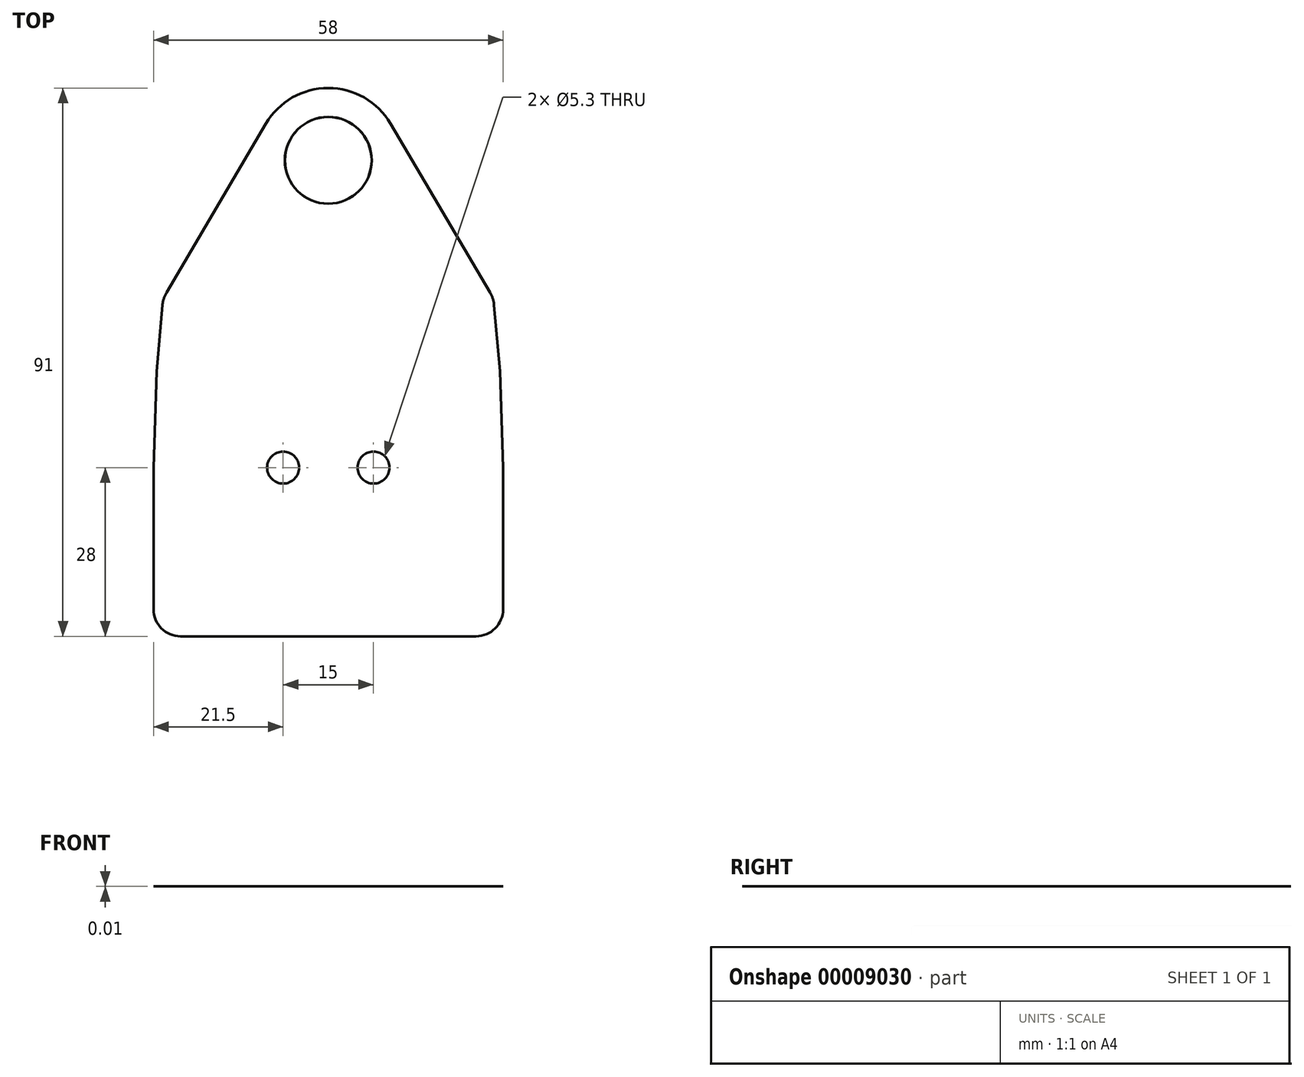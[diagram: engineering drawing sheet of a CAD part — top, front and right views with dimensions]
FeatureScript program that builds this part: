
annotation { "Feature Type Name" : "Feature", "Feature Type Description" : "" }
export const myFeature = defineFeature(function(context is Context, id is Id, definition is map)
    precondition{}
    {
        {
            var Q0;
            Q0=qCreatedBy(makeId("Top.planeOp"),FACE);
            var sketch = newSketch(context, id + "F0", { "sketchPlane" : qUnion([Q0])});
            skCircle(sketch, "E0", {"center": v(-7.5, 0) * mm, "radius": 2.65 * mm});
            skCircle(sketch, "E1", {"center": v(7.5, 0) * mm, "radius": 2.65 * mm});
            skLineSegment(sketch, "E2", {"start": v(-24.5, -28) * mm, "end": v(24.5, -28) * mm});
            skLineSegment(sketch, "E3", {"start": v(-29, -23.5) * mm, "end": v(-29, 0) * mm});
            skLineSegment(sketch, "E4", {"start": v(-29, 0) * mm, "end": v(-28.5, 16) * mm});
            skLineSegment(sketch, "E5", {"start": v(29, -23.5) * mm, "end": v(29, 0) * mm});
            skLineSegment(sketch, "E6", {"start": v(-7.5, 0) * mm, "end": v(7.5, 0) * mm, "construction": true});
            skLineSegment(sketch, "E7", {"start": v(-29, 0) * mm, "end": v(29, 0) * mm, "construction": true});
            skLineSegment(sketch, "E8", {"start": v(0, 32) * mm, "end": v(-22.68, 31.5) * mm, "construction": true});
            skPoint(sketch, "E9", {"position": v(0, -28) * mm});
            skArc(sketch, "E10", {"start": v(-29, -23.5) * mm, "mid": v(-27.68, -26.68) * mm, "end": v(-24.5, -28) * mm});
            skArc(sketch, "E11", {"start": v(24.5, -28) * mm, "mid": v(27.68, -26.68) * mm, "end": v(29, -23.5) * mm});
            skLineSegment(sketch, "E12", {"start": v(29, 0) * mm, "end": v(28.5, 16) * mm});
            skLineSegment(sketch, "E13", {"start": v(28.5, 16) * mm, "end": v(27.5, 27) * mm});
            skLineSegment(sketch, "E14", {"start": v(-28.5, 16) * mm, "end": v(-27.5, 27) * mm});
            skLineSegment(sketch, "E15", {"start": v(-28.5, 16) * mm, "end": v(28.5, 16) * mm, "construction": true});
            skPoint(sketch, "E16", {"position": v(0, 16) * mm});
            skLineSegment(sketch, "E17", {"start": v(-27.5, 27) * mm, "end": v(27.5, 27) * mm, "construction": true});
            skPoint(sketch, "E18", {"position": v(0, 27) * mm});
            skLineSegment(sketch, "E19", {"start": v(0, 32) * mm, "end": v(22.68, 31.5) * mm, "construction": true});
            skCircle(sketch, "E20", {"center": v(0, 51) * mm, "radius": 3.2 * mm});
            skArc(sketch, "E21", {"start": v(-22.68, 31.5) * mm, "mid": v(-25.95, 30.17) * mm, "end": v(-27.5, 27) * mm, "construction": true});
            skArc(sketch, "E22", {"start": v(27.5, 27) * mm, "mid": v(25.95, 30.17) * mm, "end": v(22.68, 31.5) * mm, "construction": true});
            skLineSegment(sketch, "E23", {"start": v(-10.34, 57.09) * mm, "end": v(-26.84, 29.06) * mm});
            skLineSegment(sketch, "E24", {"start": v(10.34, 57.09) * mm, "end": v(26.84, 29.06) * mm});
            skArc(sketch, "E25", {"start": v(-26.84, 29.06) * mm, "mid": v(-27.28, 28.07) * mm, "end": v(-27.5, 27) * mm});
            skArc(sketch, "E26", {"start": v(27.5, 27) * mm, "mid": v(27.28, 28.07) * mm, "end": v(26.84, 29.06) * mm});
            skArc(sketch, "E27", {"start": v(10.34, 57.09) * mm, "mid": v(0, 63) * mm, "end": v(-10.34, 57.09) * mm});
            skSolve(sketch);
        }
        {
            var Q0;
            Q0 = qSketchRegion(id + "F0", true);
            extrude(context, id + "F1", {"entities" : qUnion([Q0]), "depth" : 3 / 406.4 * mm});
        }
        {
            var Q0;
            Q0=makeQuery(id+"F1.opExtrude","CAP_EDGE",EDGE,{"disambiguationData":[OSD([sQuery(id+"F0.wireOp",EDGE,"E20")])],"isStart":false});
            chamfer(context, id + "F2", {"entities" : qUnion([Q0]), "width" : 4 * mm, "tangentPropagation" : true});
        }
    });
